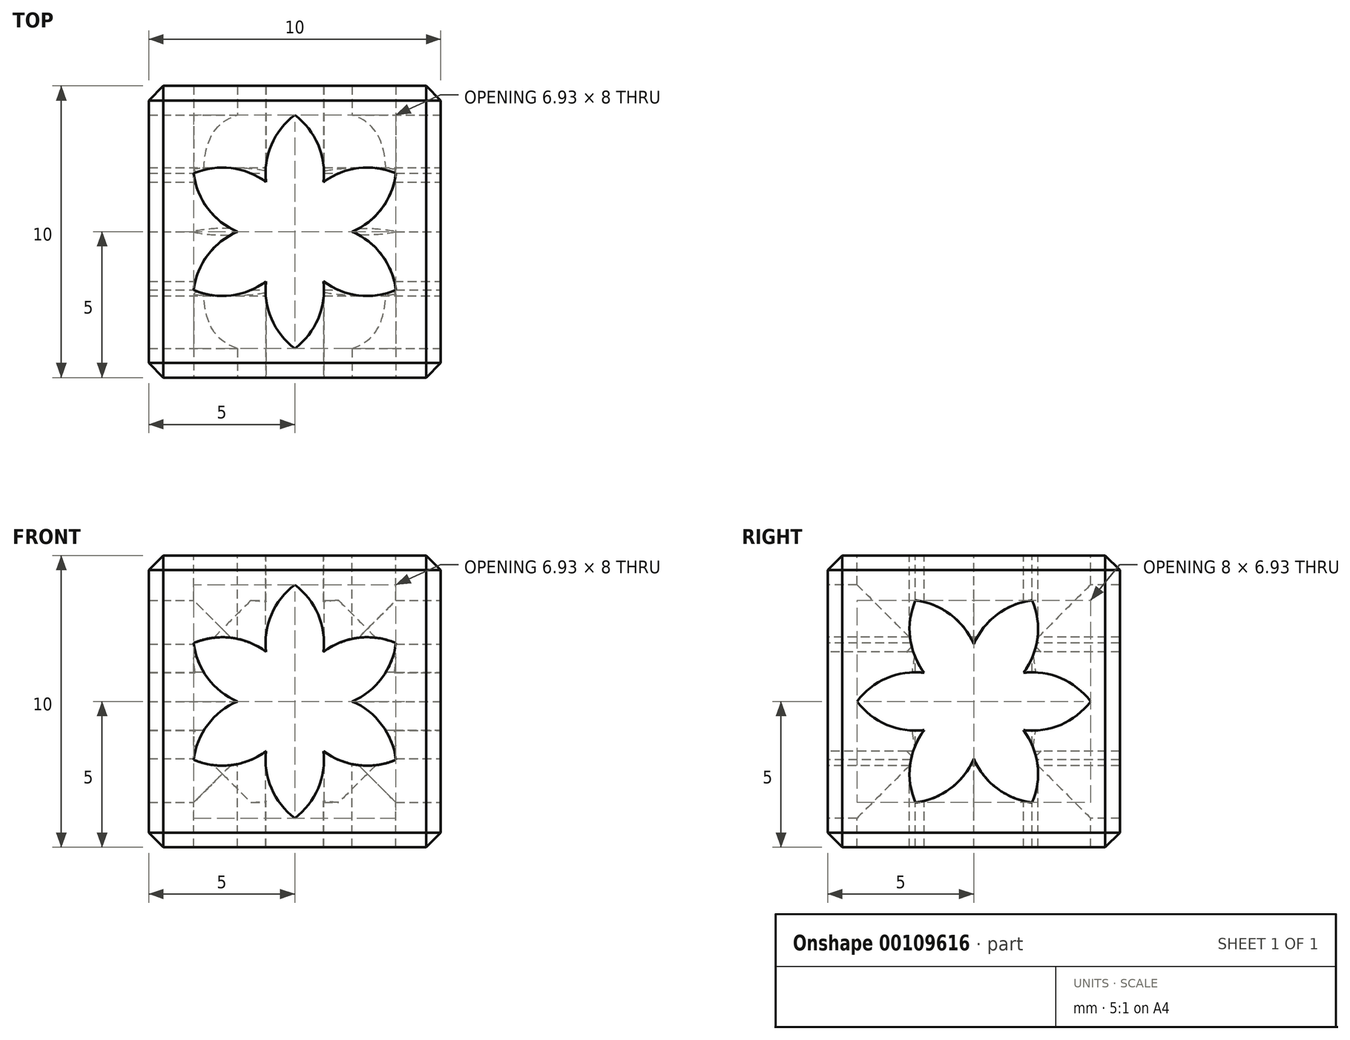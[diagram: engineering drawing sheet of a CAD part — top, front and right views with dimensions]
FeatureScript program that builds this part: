
annotation { "Feature Type Name" : "Feature", "Feature Type Description" : "" }
export const myFeature = defineFeature(function(context is Context, id is Id, definition is map)
    precondition{}
    {
        {
            var Q0;
            Q0=qCreatedBy(makeId("Top.planeOp"),FACE);
            var sketch = newSketch(context, id + "F0", { "sketchPlane" : qUnion([Q0])});
            skLineSegment(sketch, "E0.bottom", {"start": v(5, 5) * mm, "end": v(-5, 5) * mm});
            skLineSegment(sketch, "E0.top", {"start": v(5, -5) * mm, "end": v(-5, -5) * mm});
            skLineSegment(sketch, "E0.left", {"start": v(5, 5) * mm, "end": v(5, -5) * mm});
            skLineSegment(sketch, "E0.right", {"start": v(-5, 5) * mm, "end": v(-5, -5) * mm});
            skPoint(sketch, "E0.middle", {"position": v(0, 0) * mm});
            skSolve(sketch);
        }
        {
            var Q0;
            Q0=makeQuery(id+"F0.imprint","IMPRINT",FACE,{"disambiguationData":[TD([[makeQuery(id+"F0.imprint","IMPRINT",EDGE,{"derivedFrom":sQuery(id+"F0.wireOp",EDGE,"E0.bottom")}),1.0]])]});
            extrude(context, id + "F1", {"entities" : qUnion([Q0]), "depth" : 10 * mm});
        }
        {
            var Q0;
            Q0=makeQuery(id+"F1.opExtrude","CAP_FACE",FACE,{"disambiguationData":[OSD([sQuery(id+"F0.wireOp",EDGE,"E0.bottom"),sQuery(id+"F0.wireOp",EDGE,"E0.top"),sQuery(id+"F0.wireOp",EDGE,"E0.left"),sQuery(id+"F0.wireOp",EDGE,"E0.right")])],"isStart":false});
            var sketch = newSketch(context, id + "F2", { "sketchPlane" : qUnion([Q0])});
            skPoint(sketch, "E1", {"position": v(0, 0) * mm});
            skSolve(sketch);
        }
        {
            var Q0;
            Q0=makeQuery(id+"F1.opExtrude","SWEPT_FACE",FACE,{"disambiguationData":[OSD([sQuery(id+"F0.wireOp",EDGE,"E0.left")])]});
            var sketch = newSketch(context, id + "F3", { "sketchPlane" : qUnion([Q0])});
            skPoint(sketch, "E2", {"position": v(0, 5) * mm});
            skPoint(sketch, "E2.positionSnap0", {"position": v(-5, 5) * mm});
            skPoint(sketch, "E2.positionSnap1", {"position": v(0, 10) * mm});
            skSolve(sketch);
        }
        {
            var Q0;
            Q0=makeQuery(id+"F1.opExtrude","SWEPT_EDGE",EDGE,{"disambiguationData":[OSD([sQuery(id+"F0.wireOp",EDGE,"E0.top"),sQuery(id+"F0.wireOp",EDGE,"E0.left")])]});
            var Q1;
            Q1=makeQuery(id+"F1.opExtrude","CAP_EDGE",EDGE,{"disambiguationData":[OSD([sQuery(id+"F0.wireOp",EDGE,"E0.left")])],"isStart":false});
            var Q2;
            Q2=makeQuery(id+"F1.opExtrude","CAP_EDGE",EDGE,{"disambiguationData":[OSD([sQuery(id+"F0.wireOp",EDGE,"E0.top")])],"isStart":false});
            var Q3;
            Q3=makeQuery(id+"F1.opExtrude","CAP_EDGE",EDGE,{"disambiguationData":[OSD([sQuery(id+"F0.wireOp",EDGE,"E0.bottom")])],"isStart":false});
            var Q4;
            Q4=makeQuery(id+"F1.opExtrude","CAP_EDGE",EDGE,{"disambiguationData":[OSD([sQuery(id+"F0.wireOp",EDGE,"E0.right")])],"isStart":false});
            var Q5;
            Q5=makeQuery(id+"F1.opExtrude","CAP_EDGE",EDGE,{"disambiguationData":[OSD([sQuery(id+"F0.wireOp",EDGE,"E0.top")])],"isStart":true});
            var Q6;
            Q6=makeQuery(id+"F1.opExtrude","SWEPT_EDGE",EDGE,{"disambiguationData":[OSD([sQuery(id+"F0.wireOp",EDGE,"E0.top"),sQuery(id+"F0.wireOp",EDGE,"E0.right")])]});
            var Q7;
            Q7=makeQuery(id+"F1.opExtrude","CAP_EDGE",EDGE,{"disambiguationData":[OSD([sQuery(id+"F0.wireOp",EDGE,"E0.left")])],"isStart":true});
            var Q8;
            Q8=makeQuery(id+"F1.opExtrude","SWEPT_EDGE",EDGE,{"disambiguationData":[OSD([sQuery(id+"F0.wireOp",EDGE,"E0.bottom"),sQuery(id+"F0.wireOp",EDGE,"E0.left")])]});
            var Q9;
            Q9=makeQuery(id+"F1.opExtrude","CAP_EDGE",EDGE,{"disambiguationData":[OSD([sQuery(id+"F0.wireOp",EDGE,"E0.bottom")])],"isStart":true});
            var Q10;
            Q10=makeQuery(id+"F1.opExtrude","SWEPT_EDGE",EDGE,{"disambiguationData":[OSD([sQuery(id+"F0.wireOp",EDGE,"E0.bottom"),sQuery(id+"F0.wireOp",EDGE,"E0.right")])]});
            var Q11;
            Q11=makeQuery(id+"F1.opExtrude","CAP_EDGE",EDGE,{"disambiguationData":[OSD([sQuery(id+"F0.wireOp",EDGE,"E0.right")])],"isStart":true});
            chamfer(context, id + "F4", {"entities" : qUnion([Q0, Q1, Q2, Q3, Q4, Q5, Q6, Q7, Q8, Q9, Q10, Q11]), "width" : 0.5 * mm, "tangentPropagation" : true});
        }
        {
            var Q0;
            Q0=makeQuery(id+"F1.opExtrude","SWEPT_FACE",FACE,{"disambiguationData":[OSD([sQuery(id+"F0.wireOp",EDGE,"E0.top")])]});
            var sketch = newSketch(context, id + "F5", { "sketchPlane" : qUnion([Q0])});
            skPoint(sketch, "E3", {"position": v(0, 10) * mm});
            skPoint(sketch, "E4", {"position": v(0, 5) * mm});
            skPoint(sketch, "E4.positionSnap0", {"position": v(5, 5) * mm});
            skPoint(sketch, "E5", {"position": v(0, 9) * mm});
            skArc(sketch, "E6", {"start": v(0, 9) * mm, "mid": v(-0.8, 7.98) * mm, "end": v(-0.98, 6.7) * mm});
            skArc(sketch, "E7", {"start": v(0.98, 6.7) * mm, "mid": v(0.8, 7.98) * mm, "end": v(0, 9) * mm});
            skArc(sketch, "E8.1.0", {"start": v(-0.98, 6.7) * mm, "mid": v(-2.18, 7.18) * mm, "end": v(-3.46, 7) * mm});
            skArc(sketch, "E8.1.1", {"start": v(-3.46, 7) * mm, "mid": v(-2.98, 5.8) * mm, "end": v(-1.96, 5) * mm});
            skArc(sketch, "E8.2.0", {"start": v(-1.96, 5) * mm, "mid": v(-2.98, 4.2) * mm, "end": v(-3.46, 3) * mm});
            skArc(sketch, "E8.2.1", {"start": v(-3.46, 3) * mm, "mid": v(-2.18, 2.82) * mm, "end": v(-0.98, 3.3) * mm});
            skArc(sketch, "E8.3.0", {"start": v(-0.98, 3.3) * mm, "mid": v(-0.8, 2.02) * mm, "end": v(0, 1) * mm});
            skArc(sketch, "E8.3.1", {"start": v(0, 1) * mm, "mid": v(0.8, 2.02) * mm, "end": v(0.98, 3.3) * mm});
            skArc(sketch, "E8.4.0", {"start": v(0.98, 3.3) * mm, "mid": v(2.18, 2.82) * mm, "end": v(3.46, 3) * mm});
            skArc(sketch, "E8.4.1", {"start": v(3.46, 3) * mm, "mid": v(2.98, 4.2) * mm, "end": v(1.96, 5) * mm});
            skArc(sketch, "E9.2.5.0", {"start": v(1.96, 5) * mm, "mid": v(2.98, 5.8) * mm, "end": v(3.46, 7) * mm});
            skArc(sketch, "E9.4.5.0", {"start": v(3.46, 7) * mm, "mid": v(2.18, 7.18) * mm, "end": v(0.98, 6.7) * mm});
            skSolve(sketch);
        }
        {
            var Q0;
            Q0=makeQuery(id+"F5.imprint","IMPRINT",FACE,{"disambiguationData":[TD([[makeQuery(id+"F5.imprint","IMPRINT",EDGE,{"derivedFrom":sQuery(id+"F5.wireOp",EDGE,"E6")}),1.0]])]});
            extrude(context, id + "F6", {"entities" : qUnion([Q0]), "operationType" : NewBodyOperationType.REMOVE, "oppositeDirection" : true, "depth" : 25 * mm});
        }
        {
            var Q0;
            Q0=makeQuery(id+"F2.imprint","IMPRINT",FACE,{"disambiguationData":[TD([[makeQuery(id+"F2.imprint","IMPRINT",EDGE,{"derivedFrom":makeQuery(id+"F1.opExtrude","CAP_EDGE",EDGE,{"disambiguationData":[OSD([sQuery(id+"F0.wireOp",EDGE,"E0.bottom")])],"isStart":false})}),1.0]])]});
            var sketch = newSketch(context, id + "F7", { "sketchPlane" : qUnion([Q0])});
            skPoint(sketch, "E10", {"position": v(0, 0) * mm});
            skPoint(sketch, "E11", {"position": v(0, 4) * mm});
            skArc(sketch, "E12", {"start": v(0, 4) * mm, "mid": v(-0.8, 2.98) * mm, "end": v(-0.98, 1.7) * mm});
            skArc(sketch, "E13", {"start": v(0.98, 1.7) * mm, "mid": v(0.8, 2.98) * mm, "end": v(0, 4) * mm});
            skArc(sketch, "E14.1.0", {"start": v(-0.98, 1.7) * mm, "mid": v(-2.18, 2.18) * mm, "end": v(-3.46, 2) * mm});
            skArc(sketch, "E14.1.1", {"start": v(-3.46, 2) * mm, "mid": v(-2.98, 0.8) * mm, "end": v(-1.96, 0) * mm});
            skArc(sketch, "E14.2.0", {"start": v(-1.96, 0) * mm, "mid": v(-2.98, -0.8) * mm, "end": v(-3.46, -2) * mm});
            skArc(sketch, "E14.2.1", {"start": v(-3.46, -2) * mm, "mid": v(-2.18, -2.18) * mm, "end": v(-0.98, -1.7) * mm});
            skArc(sketch, "E14.3.0", {"start": v(-0.98, -1.7) * mm, "mid": v(-0.8, -2.98) * mm, "end": v(0, -4) * mm});
            skArc(sketch, "E14.3.1", {"start": v(0, -4) * mm, "mid": v(0.8, -2.98) * mm, "end": v(0.98, -1.7) * mm});
            skArc(sketch, "E14.4.0", {"start": v(0.98, -1.7) * mm, "mid": v(2.18, -2.18) * mm, "end": v(3.46, -2) * mm});
            skArc(sketch, "E14.4.1", {"start": v(3.46, -2) * mm, "mid": v(2.98, -0.8) * mm, "end": v(1.96, 0) * mm});
            skArc(sketch, "E14.5.0", {"start": v(1.96, 0) * mm, "mid": v(2.98, 0.8) * mm, "end": v(3.46, 2) * mm});
            skArc(sketch, "E14.5.1", {"start": v(3.46, 2) * mm, "mid": v(2.18, 2.18) * mm, "end": v(0.98, 1.7) * mm});
            skSolve(sketch);
        }
        {
            var Q0;
            Q0=makeQuery(id+"F7.imprint","IMPRINT",FACE,{"disambiguationData":[TD([[makeQuery(id+"F7.imprint","IMPRINT",EDGE,{"derivedFrom":sQuery(id+"F7.wireOp",EDGE,"E12")}),1.0]])]});
            extrude(context, id + "F8", {"entities" : qUnion([Q0]), "operationType" : NewBodyOperationType.REMOVE, "oppositeDirection" : true, "depth" : 25 * mm});
        }
        {
            var Q0;
            {var subQ0=sQuery(id+"F0.wireOp",EDGE,"E0.left");Q0=makeQuery(id+"F3.imprint","IMPRINT",FACE,{"disambiguationData":[TD([[makeQuery(id+"F3.imprint","IMPRINT",EDGE,{"derivedFrom":makeQuery(id+"F1.opExtrude","CAP_EDGE",EDGE,{"disambiguationData":[OSD([subQ0])],"isStart":true})}),-1.0]])]});}
            var sketch = newSketch(context, id + "F9", { "sketchPlane" : qUnion([Q0])});
            skPoint(sketch, "E15", {"position": v(0, 5) * mm});
            skPoint(sketch, "E16", {"position": v(4, 5) * mm});
            skArc(sketch, "E17", {"start": v(4, 5) * mm, "mid": v(2.98, 5.8) * mm, "end": v(1.7, 5.98) * mm});
            skArc(sketch, "E18", {"start": v(1.7, 4.02) * mm, "mid": v(2.98, 4.2) * mm, "end": v(4, 5) * mm});
            skArc(sketch, "E19.1.0", {"start": v(1.7, 5.98) * mm, "mid": v(2.18, 7.18) * mm, "end": v(2, 8.46) * mm});
            skArc(sketch, "E19.1.1", {"start": v(2, 8.46) * mm, "mid": v(0.8, 7.98) * mm, "end": v(0, 6.96) * mm});
            skArc(sketch, "E19.2.0", {"start": v(0, 6.96) * mm, "mid": v(-0.8, 7.98) * mm, "end": v(-2, 8.46) * mm});
            skArc(sketch, "E19.2.1", {"start": v(-2, 8.46) * mm, "mid": v(-2.18, 7.18) * mm, "end": v(-1.7, 5.98) * mm});
            skArc(sketch, "E19.3.0", {"start": v(-1.7, 5.98) * mm, "mid": v(-2.98, 5.8) * mm, "end": v(-4, 5) * mm});
            skArc(sketch, "E19.3.1", {"start": v(-4, 5) * mm, "mid": v(-2.98, 4.2) * mm, "end": v(-1.7, 4.02) * mm});
            skArc(sketch, "E19.4.0", {"start": v(-1.7, 4.02) * mm, "mid": v(-2.18, 2.82) * mm, "end": v(-2, 1.54) * mm});
            skArc(sketch, "E19.4.1", {"start": v(-2, 1.54) * mm, "mid": v(-0.8, 2.02) * mm, "end": v(0, 3.04) * mm});
            skArc(sketch, "E19.5.0", {"start": v(0, 3.04) * mm, "mid": v(0.8, 2.02) * mm, "end": v(2, 1.54) * mm});
            skArc(sketch, "E19.5.1", {"start": v(2, 1.54) * mm, "mid": v(2.18, 2.82) * mm, "end": v(1.7, 4.02) * mm});
            skSolve(sketch);
        }
        {
            var Q0;
            Q0=makeQuery(id+"F9.imprint","IMPRINT",FACE,{"disambiguationData":[TD([[makeQuery(id+"F9.imprint","IMPRINT",EDGE,{"derivedFrom":sQuery(id+"F9.wireOp",EDGE,"E17")}),1.0]])]});
            var Q1;
            Q1=sQuery(id+"F9.wireOp",EDGE,"E19.3.1");
            var Q2;
            Q2=sQuery(id+"F9.wireOp",EDGE,"E19.4.0");
            var Q3;
            Q3=sQuery(id+"F9.wireOp",EDGE,"E19.4.1");
            var Q4;
            Q4=sQuery(id+"F9.wireOp",EDGE,"E19.5.0");
            var Q5;
            Q5=sQuery(id+"F9.wireOp",EDGE,"E19.5.1");
            var Q6;
            Q6=sQuery(id+"F9.wireOp",EDGE,"E18");
            var Q7;
            Q7=sQuery(id+"F9.wireOp",EDGE,"E17");
            var Q8;
            Q8=sQuery(id+"F9.wireOp",EDGE,"E19.1.0");
            var Q9;
            Q9=sQuery(id+"F9.wireOp",EDGE,"E19.1.1");
            var Q10;
            Q10=sQuery(id+"F9.wireOp",EDGE,"E19.2.0");
            var Q11;
            Q11=sQuery(id+"F9.wireOp",EDGE,"E19.2.1");
            var Q12;
            Q12=sQuery(id+"F9.wireOp",EDGE,"E19.3.0");
            extrude(context, id + "F10", {"entities" : qUnion([Q0]), "operationType" : NewBodyOperationType.REMOVE, "surfaceEntities" : qUnion([Q1, Q2, Q3, Q4, Q5, Q6, Q7, Q8, Q9, Q10, Q11, Q12]), "oppositeDirection" : true, "depth" : 25 * mm});
        }
    });
